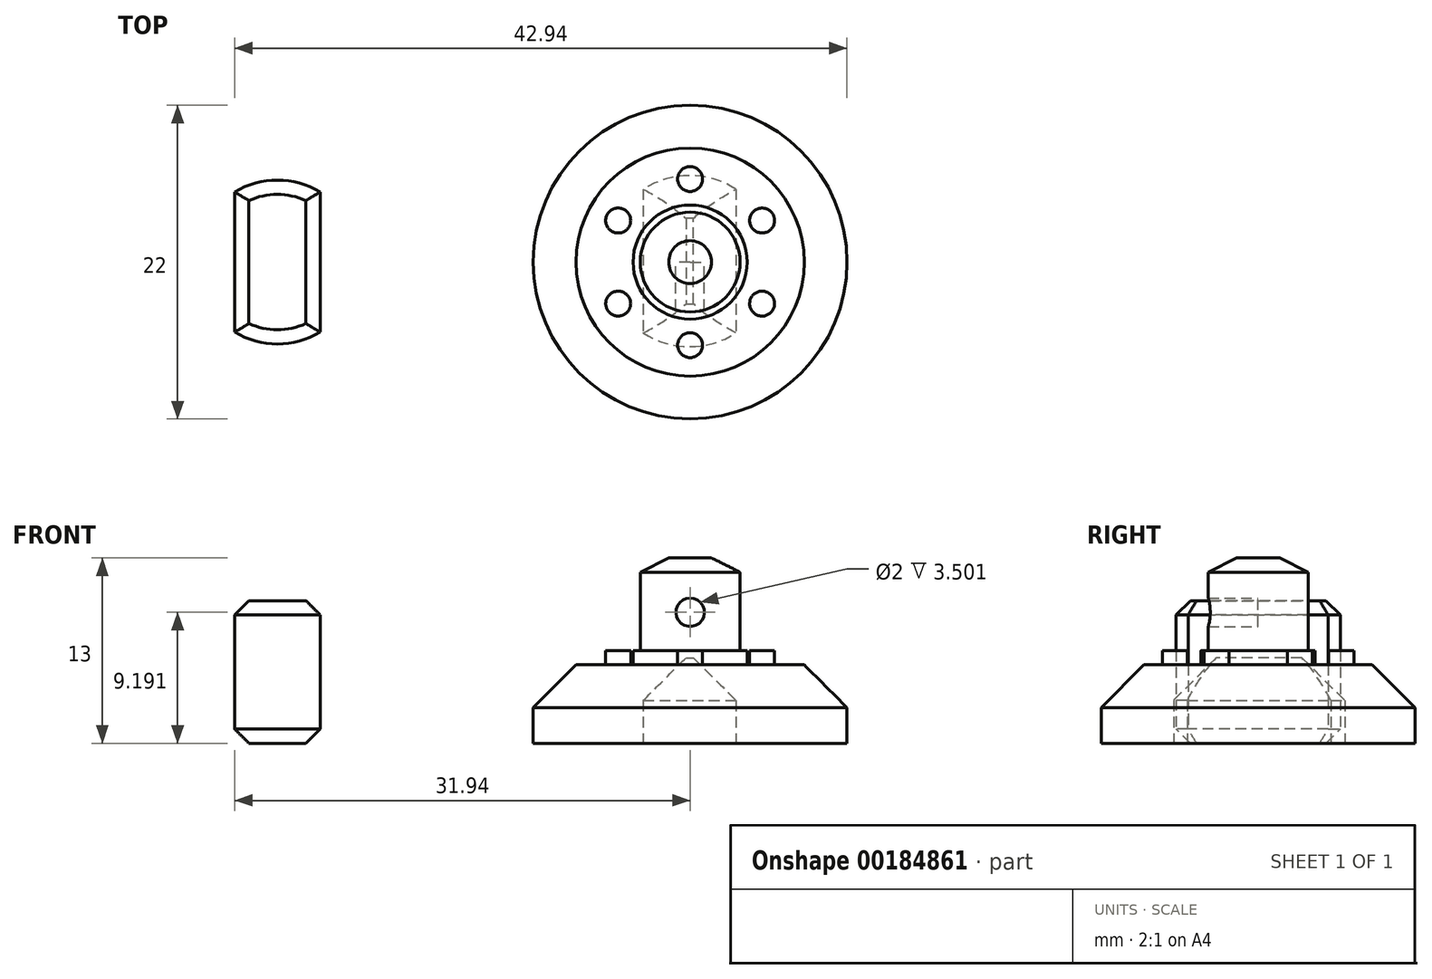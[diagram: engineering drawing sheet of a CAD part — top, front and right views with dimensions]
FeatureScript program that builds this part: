
annotation { "Feature Type Name" : "Feature", "Feature Type Description" : "" }
export const myFeature = defineFeature(function(context is Context, id is Id, definition is map)
    precondition{}
    {
        {
            var Q0;
            Q0=qCreatedBy(makeId("Top.planeOp"),FACE);
            var sketch = newSketch(context, id + "F0", { "sketchPlane" : qUnion([Q0])});
            skArc(sketch, "E0", {"start": v(-25.94, 4.9) * mm, "mid": v(-28.94, 5.75) * mm, "end": v(-31.94, 4.9) * mm});
            skLineSegment(sketch, "E1.bottom", {"start": v(-25.94, -4.9) * mm, "end": v(-31.94, -4.9) * mm});
            skLineSegment(sketch, "E1.top", {"start": v(-25.94, 4.9) * mm, "end": v(-31.94, 4.9) * mm});
            skLineSegment(sketch, "E1.left", {"start": v(-25.94, -4.9) * mm, "end": v(-25.94, 4.9) * mm});
            skLineSegment(sketch, "E1.right", {"start": v(-31.94, -4.9) * mm, "end": v(-31.94, 4.9) * mm});
            skArc(sketch, "E2.trimOffspring", {"start": v(-31.94, -4.9) * mm, "mid": v(-28.94, -5.75) * mm, "end": v(-25.94, -4.9) * mm});
            skSolve(sketch);
        }
        {
            var Q0;
            Q0 = qSketchRegion(id + "F0", true);
            extrude(context, id + "F1", {"entities" : qUnion([Q0]), "depth" : 10 * mm});
        }
        {
            var Q0;
            Q0=makeQuery(id+"F1.opExtrude","CAP_FACE",FACE,{"disambiguationData":[OSD([sQuery(id+"F0.wireOp",EDGE,"E0"),sQuery(id+"F0.wireOp",EDGE,"E1.left"),sQuery(id+"F0.wireOp",EDGE,"E1.right"),sQuery(id+"F0.wireOp",EDGE,"E2.trimOffspring")])],"isStart":false});
            var Q1;
            Q1=makeQuery(id+"F1.opExtrude","CAP_FACE",FACE,{"disambiguationData":[OSD([sQuery(id+"F0.wireOp",EDGE,"E0"),sQuery(id+"F0.wireOp",EDGE,"E1.left"),sQuery(id+"F0.wireOp",EDGE,"E1.right"),sQuery(id+"F0.wireOp",EDGE,"E2.trimOffspring")])],"isStart":true});
            chamfer(context, id + "F2", {"entities" : qUnion([Q0, Q1]), "width" : 1 * mm, "tangentPropagation" : true});
        }
        {
            var Q0;
            Q0=qCreatedBy(makeId("Top.planeOp"),FACE);
            var sketch = newSketch(context, id + "F3", { "sketchPlane" : qUnion([Q0])});
            skCircle(sketch, "E3", {"center": v(0, 0) * mm, "radius": 11 * mm});
            skSolve(sketch);
        }
        {
            var Q0;
            Q0 = qSketchRegion(id + "F3", true);
            extrude(context, id + "F4", {"entities" : qUnion([Q0]), "depth" : 5.5 * mm});
        }
        {
            var Q0;
            Q0=makeQuery(id+"F4.opExtrude","CAP_EDGE",EDGE,{"disambiguationData":[OSD([sQuery(id+"F3.wireOp",EDGE,"E3")])],"isStart":false});
            chamfer(context, id + "F5", {"entities" : qUnion([Q0]), "width" : 3 * mm, "tangentPropagation" : true});
        }
        {
            var Q0;
            Q0=qCreatedBy(makeId("Top.planeOp"),FACE);
            var sketch = newSketch(context, id + "F6", { "sketchPlane" : qUnion([Q0])});
            skCircle(sketch, "E4", {"center": v(0, -5.83) * mm, "radius": 0.88 * mm});
            skSolve(sketch);
        }
        {
            var Q0;
            Q0 = qSketchRegion(id + "F6", true);
            extrude(context, id + "F7", {"entities" : qUnion([Q0]), "depth" : 6.5 * mm});
        }
        {
            var Q0;
            Q0=makeQuery(id+"F7.opExtrude","SWEPT_BODY",BODY,{"disambiguationData":[OSD([sQuery(id+"F6.wireOp",EDGE,"E4")])]});
            var Q1;
            {var subQ0=sQuery(id+"F3.wireOp",EDGE,"E3");Q1=makeQuery(id+"F5.opChamfer","BLEND_EDGE",EDGE,{"blendedFrom":[makeQuery(id+"F4.opExtrude","CAP_EDGE",EDGE,{"disambiguationData":[OSD([subQ0])],"isStart":false}),makeQuery(id+"F4.opExtrude","CAP_FACE",FACE,{"disambiguationData":[OSD([subQ0])],"isStart":false})],"blendedInto":[makeQuery(id+"F4.opExtrude","CAP_FACE",FACE,{"disambiguationData":[OSD([subQ0])],"isStart":false})]});}
            circularPattern(context, id + "F8", {"operationType" : NewBodyOperationType.ADD, "entities" : qUnion([Q0]), "axis" : qUnion([Q1]), "angle" : 360 * degree, "instanceCount" : 6, "equalSpace" : true});
        }
        {
            var Q0;
            Q0=qCreatedBy(makeId("Top.planeOp"),FACE);
            var sketch = newSketch(context, id + "F9", { "sketchPlane" : qUnion([Q0])});
            skCircle(sketch, "E5", {"center": v(0, 0) * mm, "radius": 4 * mm});
            skSolve(sketch);
        }
        {
            var Q0;
            Q0 = qSketchRegion(id + "F9", true);
            extrude(context, id + "F10", {"entities" : qUnion([Q0]), "operationType" : NewBodyOperationType.ADD, "depth" : 6.5 * mm});
        }
        {
            var Q0;
            Q0=qCreatedBy(makeId("Top.planeOp"),FACE);
            var sketch = newSketch(context, id + "F11", { "sketchPlane" : qUnion([Q0])});
            skCircle(sketch, "E6", {"center": v(0, 0) * mm, "radius": 3.5 * mm});
            skSolve(sketch);
        }
        {
            var Q0;
            Q0 = qSketchRegion(id + "F11", true);
            extrude(context, id + "F12", {"entities" : qUnion([Q0]), "operationType" : NewBodyOperationType.ADD, "depth" : 13 * mm});
        }
        {
            var Q0;
            Q0=makeQuery(id+"F12.opExtrude","CAP_EDGE",EDGE,{"disambiguationData":[OSD([sQuery(id+"F11.wireOp",EDGE,"E6")])],"isStart":false});
            chamfer(context, id + "F13", {"entities" : qUnion([Q0]), "chamferType" : ChamferType.TWO_OFFSETS, "width1" : 2 * mm, "oppositeDirection" : false, "width2" : 1 * mm, "tangentPropagation" : true});
        }
        {
            var Q0;
            Q0=qCreatedBy(makeId("Top.planeOp"),FACE);
            var sketch = newSketch(context, id + "F14", { "sketchPlane" : qUnion([Q0])});
            skArc(sketch, "E7", {"start": v(-3.28, -4.98) * mm, "mid": v(-0.03, -5.93) * mm, "end": v(3.22, -4.98) * mm});
            skLineSegment(sketch, "E8", {"start": v(-3.28, 5.11) * mm, "end": v(-3.28, -4.98) * mm});
            skLineSegment(sketch, "E9", {"start": v(3.22, 5.11) * mm, "end": v(3.22, -4.98) * mm});
            skArc(sketch, "E10.trimOffspring", {"start": v(3.22, 5.11) * mm, "mid": v(-0.03, 6.07) * mm, "end": v(-3.28, 5.11) * mm});
            skSolve(sketch);
        }
        {
            var Q0;
            Q0 = qSketchRegion(id + "F14", true);
            var Q1;
            Q1=sQuery(id+"F14.wireOp",EDGE,"E7");
            var Q2;
            Q2=sQuery(id+"F14.wireOp",EDGE,"E8");
            var Q3;
            Q3=sQuery(id+"F14.wireOp",EDGE,"E9");
            var Q4;
            Q4=sQuery(id+"F14.wireOp",EDGE,"E10.trimOffspring");
            extrude(context, id + "F15", {"entities" : qUnion([Q0]), "surfaceEntities" : qUnion([Q1, Q2, Q3, Q4]), "depth" : 6 * mm});
        }
        {
            var Q0;
            Q0=makeQuery(id+"F15.opExtrude","CAP_FACE",FACE,{"disambiguationData":[OSD([sQuery(id+"F14.wireOp",EDGE,"E7"),sQuery(id+"F14.wireOp",EDGE,"E8"),sQuery(id+"F14.wireOp",EDGE,"E9"),sQuery(id+"F14.wireOp",EDGE,"E10.trimOffspring")])],"isStart":false});
            chamfer(context, id + "F16", {"entities" : qUnion([Q0]), "width" : 3 * mm, "tangentPropagation" : true});
        }
        {
            var Q0;
            Q0=makeQuery(id+"F15.opExtrude","SWEPT_BODY",BODY,{"disambiguationData":[OSD([sQuery(id+"F14.wireOp",EDGE,"E7"),sQuery(id+"F14.wireOp",EDGE,"E8"),sQuery(id+"F14.wireOp",EDGE,"E9"),sQuery(id+"F14.wireOp",EDGE,"E10.trimOffspring")])]});
            var Q1;
            Q1=makeQuery(id+"F4.opExtrude","SWEPT_BODY",BODY,{"disambiguationData":[OSD([sQuery(id+"F3.wireOp",EDGE,"E3")])]});
            booleanBodies(context, id + "F17", {"operationType" : BooleanOperationType.SUBTRACTION, "tools" : qUnion([Q0]), "targets" : qUnion([Q1])});
        }
        {
            var Q0;
            Q0=qCreatedBy(makeId("Front.planeOp"),FACE);
            var sketch = newSketch(context, id + "F18", { "sketchPlane" : qUnion([Q0])});
            skCircle(sketch, "E11", {"center": v(0, 9.2) * mm, "radius": 1 * mm});
            skSolve(sketch);
        }
        {
            var Q0;
            Q0 = qSketchRegion(id + "F18", true);
            extrude(context, id + "F19", {"entities" : qUnion([Q0]), "operationType" : NewBodyOperationType.REMOVE, "depth" : 4 * mm});
        }
    });
